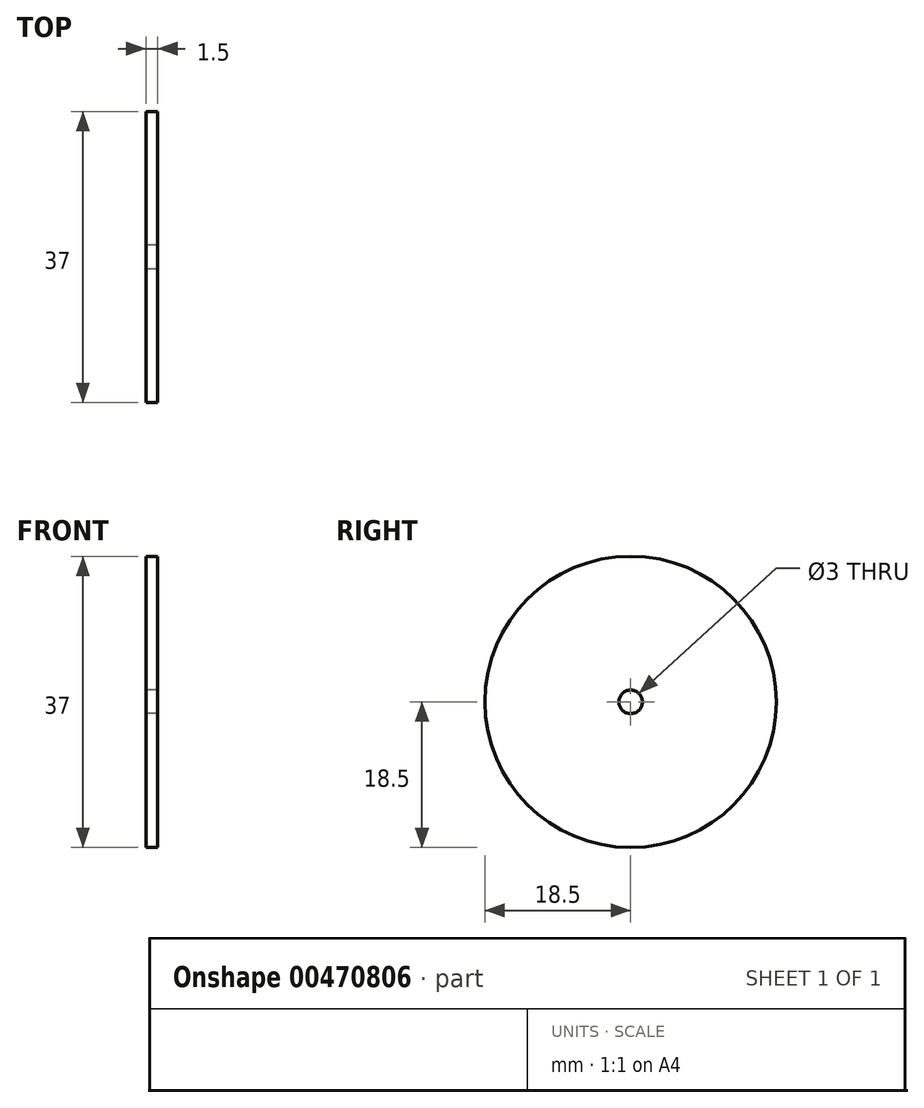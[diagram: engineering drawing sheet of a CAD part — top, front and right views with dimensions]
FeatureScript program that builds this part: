
annotation { "Feature Type Name" : "Feature", "Feature Type Description" : "" }
export const myFeature = defineFeature(function(context is Context, id is Id, definition is map)
    precondition{}
    {
        {
            var Q0;
            Q0=qCreatedBy(makeId("Right.planeOp"),FACE);
            var sketch = newSketch(context, id + "F0", { "sketchPlane" : qUnion([Q0])});
            skCircle(sketch, "E0", {"center": v(0, 0) * mm, "radius": 18.5 * mm});
            skCircle(sketch, "E1", {"center": v(0, 0) * mm, "radius": 1.5 * mm});
            skSolve(sketch);
        }
        {
            var Q0;
            Q0=makeQuery(id+"F0.imprint","IMPRINT",FACE,{"disambiguationData":[TD([[makeQuery(id+"F0.imprint","IMPRINT",EDGE,{"derivedFrom":sQuery(id+"F0.wireOp",EDGE,"E0")}),1.0]])]});
            extrude(context, id + "F1", {"entities" : qUnion([Q0]), "endBound" : BoundingType.SYMMETRIC, "depth" : 1.5 * mm});
        }
    });
